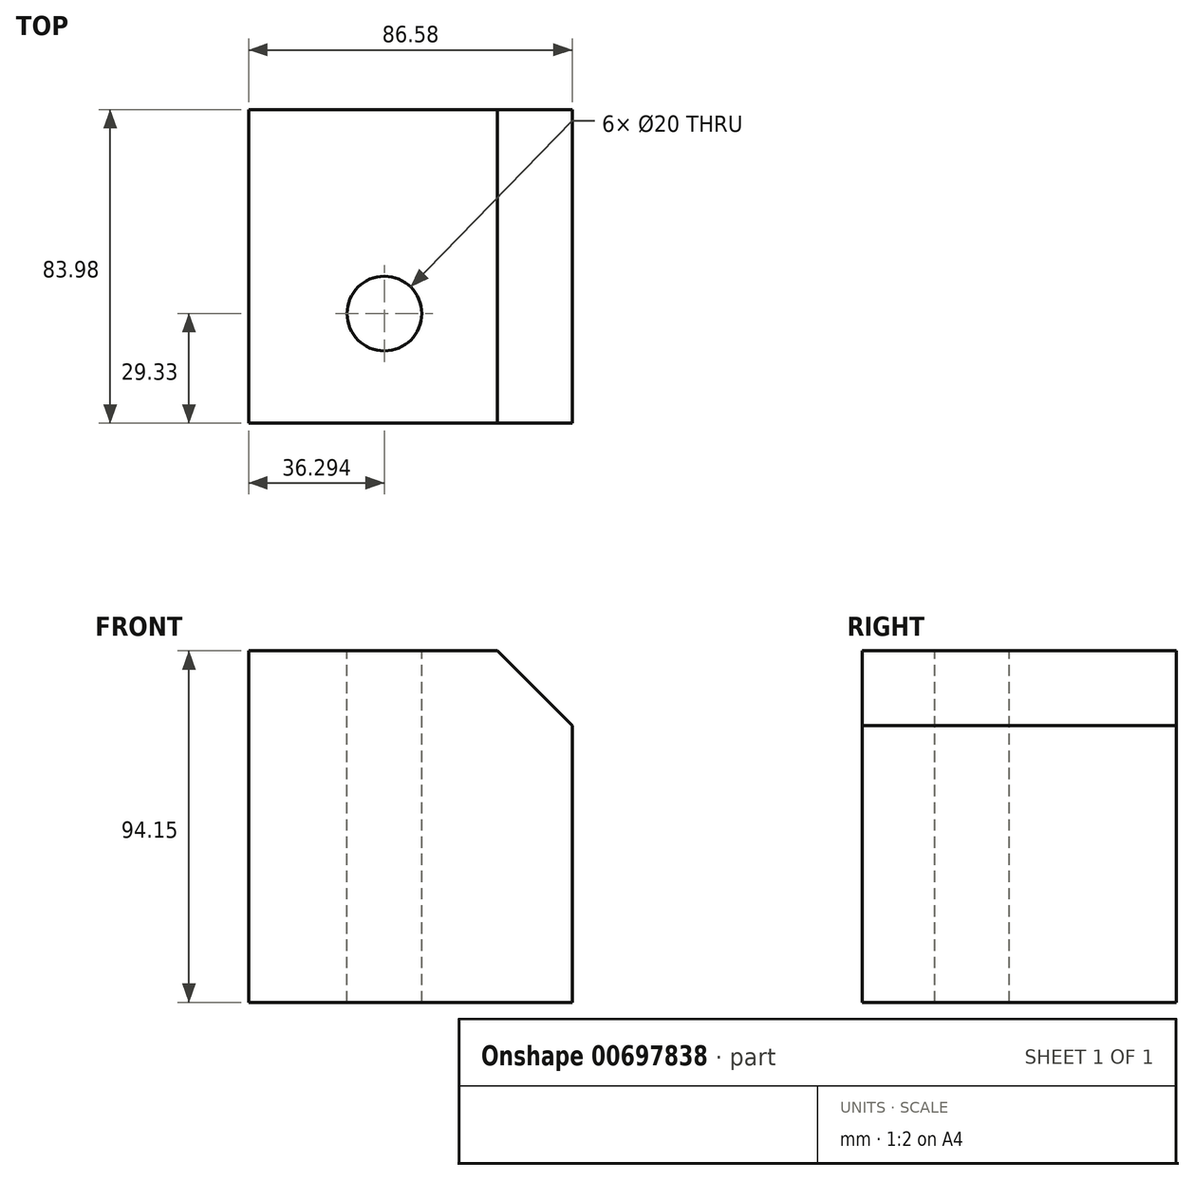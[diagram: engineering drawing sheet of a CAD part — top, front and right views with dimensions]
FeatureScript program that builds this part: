
annotation { "Feature Type Name" : "Feature", "Feature Type Description" : "" }
export const myFeature = defineFeature(function(context is Context, id is Id, definition is map)
    precondition{}
    {
        {
            var Q0;
            Q0=qCreatedBy(makeId("Top.planeOp"),FACE);
            var sketch = newSketch(context, id + "F0", { "sketchPlane" : qUnion([Q0])});
            skLineSegment(sketch, "E0.bottom", {"start": v(64.74, 54.65) * mm, "end": v(-21.84, 54.65) * mm});
            skLineSegment(sketch, "E0.top", {"start": v(64.74, -29.33) * mm, "end": v(-21.84, -29.33) * mm});
            skLineSegment(sketch, "E0.left", {"start": v(64.74, 54.65) * mm, "end": v(64.74, -29.33) * mm});
            skLineSegment(sketch, "E0.right", {"start": v(-21.84, 54.65) * mm, "end": v(-21.84, -29.33) * mm});
            skSolve(sketch);
        }
        {
            var Q0;
            Q0=makeQuery(id+"F0.imprint","IMPRINT",FACE,{"disambiguationData":[TD([[makeQuery(id+"F0.imprint","IMPRINT",EDGE,{"derivedFrom":sQuery(id+"F0.wireOp",EDGE,"E0.bottom")}),1.0]])]});
            extrude(context, id + "F1", {"entities" : qUnion([Q0]), "depth" : 94.15 * mm, "offsetDistance" : 25.4 * mm});
        }
        {
            var Q0;
            Q0=makeQuery(id+"F1.opExtrude","CAP_EDGE",EDGE,{"disambiguationData":[OSD([sQuery(id+"F0.wireOp",EDGE,"E0.left")])],"isStart":false});
            chamfer(context, id + "F2", {"entities" : qUnion([Q0]), "width" : 20 * mm, "tangentPropagation" : true});
        }
        {
            var Q0;
            Q0=makeQuery(id+"F1.opExtrude","CAP_FACE",FACE,{"disambiguationData":[OSD([sQuery(id+"F0.wireOp",EDGE,"E0.bottom"),sQuery(id+"F0.wireOp",EDGE,"E0.top"),sQuery(id+"F0.wireOp",EDGE,"E0.left"),sQuery(id+"F0.wireOp",EDGE,"E0.right")])],"isStart":false});
            var sketch = newSketch(context, id + "F3", { "sketchPlane" : qUnion([Q0])});
            skPoint(sketch, "E1", {"position": v(14.45, 0) * mm});
            skSolve(sketch);
        }
        {
            var Q0;
            Q0=sQuery(id+"F3.wireOp",VERTEX,"E1");
            var Q1;
            Q1=makeQuery(id+"F1.opExtrude","SWEPT_BODY",BODY,{"disambiguationData":[OSD([sQuery(id+"F0.wireOp",EDGE,"E0.bottom"),sQuery(id+"F0.wireOp",EDGE,"E0.top"),sQuery(id+"F0.wireOp",EDGE,"E0.left"),sQuery(id+"F0.wireOp",EDGE,"E0.right")])]});
            hole(context, id + "F4", {"style" : HoleStyle.SIMPLE, "endStyle" : HoleEndStyle.THROUGH, "holeDiameter" : 20 * mm, "majorDiameter" : 5 * mm, "isTappedThrough" : true, "tappedDepth" : 12 * mm, "tapClearance" : 3, "locations" : qUnion([Q0]), "scope" : qUnion([Q1])});
        }
    });
